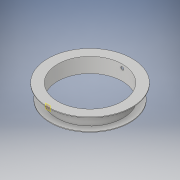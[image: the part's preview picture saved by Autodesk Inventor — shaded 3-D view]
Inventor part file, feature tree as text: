
AUTODESK INVENTOR PART (.ipt)
format: ipt  version: 2017 (Build 210142000, 142)  size: 143,360 bytes
history: native  units: in
note: dims shown in document units (in); Inventor stores cm internally (conversion verified against a paired STEP export)
features: sketch x2, revolve x1, plane x1, extrude x1
ambient origin geometry x8: Origin, YZ Plane, XZ Plane, XY Plane, X Axis, Y Axis, Z Axis, Center Point
bodies: Solid1 (feature_tree)
feature tree (5):
  revolve  "Revolution1"  [1 undecoded]
  plane  "Work Plane1"
  extrude  "Extrusion1"  Depth=0.125in
  sketch  "Sketch1"  dims[d0=2.0in d1=5.4375in]
  sketch  "Sketch2"  dims[d2=1.25in d3=0.125in d4=0.125in d5=2.25in d6=1.5in d7=0.125in d8=90.0deg d9=0.5in d10=1.75in d11=1.0in d12=0.0in]
note: 1 required parameter value undecoded (feature->parameter linkage not recoverable at this tier; creation-order binding heuristic only, values carry confidence <= 0.55)
